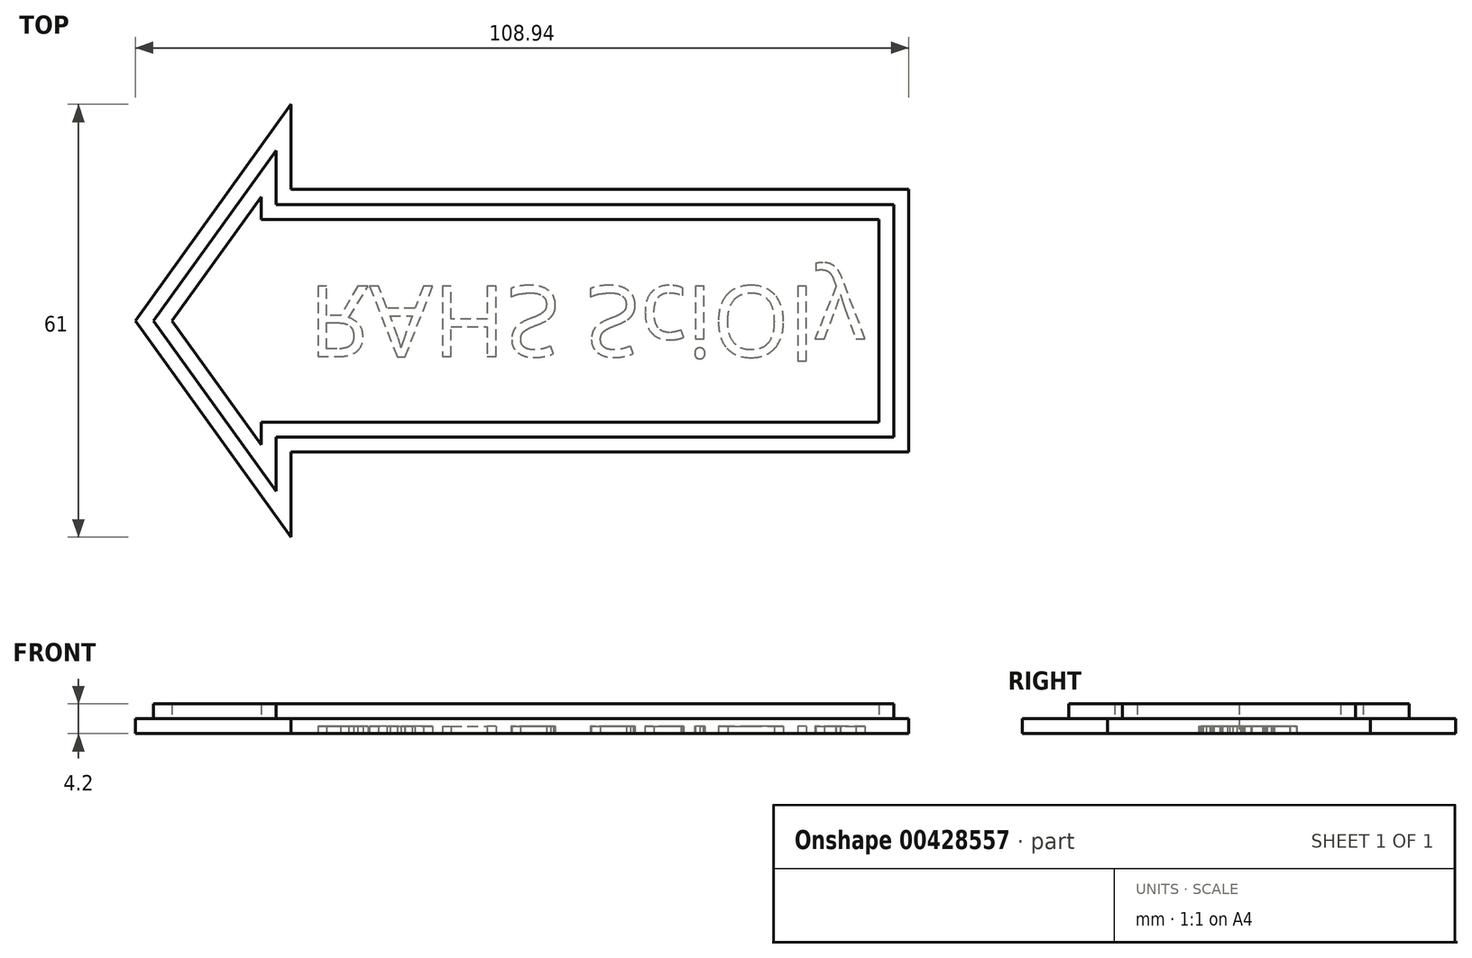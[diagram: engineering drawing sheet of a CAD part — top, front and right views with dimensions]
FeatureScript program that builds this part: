
annotation { "Feature Type Name" : "Feature", "Feature Type Description" : "" }
export const myFeature = defineFeature(function(context is Context, id is Id, definition is map)
    precondition{}
    {
        {
            var Q0;
            Q0=qCreatedBy(makeId("Top.planeOp"),FACE);
            var sketch = newSketch(context, id + "F0", { "sketchPlane" : qUnion([Q0])});
            skLineSegment(sketch, "E0.0", {"start": v(61.6, 18.5) * mm, "end": v(61.6, -18.5) * mm});
            skLineSegment(sketch, "E0.1", {"start": v(-25.4, 18.5) * mm, "end": v(61.6, 18.5) * mm});
            skLineSegment(sketch, "E0.3", {"start": v(-25.4, -18.5) * mm, "end": v(61.6, -18.5) * mm});
            skLineSegment(sketch, "E1", {"start": v(-25.4, 18.5) * mm, "end": v(-25.4, 30.5) * mm});
            skLineSegment(sketch, "E2", {"start": v(-25.4, 30.5) * mm, "end": v(-47.35, 0) * mm});
            skLineSegment(sketch, "E3", {"start": v(-47.35, 0) * mm, "end": v(-25.4, -30.5) * mm});
            skLineSegment(sketch, "E4", {"start": v(-25.4, -30.5) * mm, "end": v(-25.4, -18.5) * mm});
            skPoint(sketch, "E5", {"position": v(61.6, 0) * mm});
            skSolve(sketch);
        }
        {
            var Q0;
            Q0=makeQuery(id+"F0.imprint","IMPRINT",FACE,{"disambiguationData":[TD([[makeQuery(id+"F0.imprint","IMPRINT",EDGE,{"derivedFrom":sQuery(id+"F0.wireOp",EDGE,"E0.0")}),-1.0]])]});
            extrude(context, id + "F1", {"entities" : qUnion([Q0]), "depth" : 2.1 * mm});
        }
        {
            var Q0;
            Q0=makeQuery(id+"F1.opExtrude","CAP_FACE",FACE,{"disambiguationData":[OSD([sQuery(id+"F0.wireOp",EDGE,"E0.0"),sQuery(id+"F0.wireOp",EDGE,"E0.1"),sQuery(id+"F0.wireOp",EDGE,"E0.3"),sQuery(id+"F0.wireOp",EDGE,"E1"),sQuery(id+"F0.wireOp",EDGE,"E2"),sQuery(id+"F0.wireOp",EDGE,"E3"),sQuery(id+"F0.wireOp",EDGE,"E4")])],"isStart":false});
            var sketch = newSketch(context, id + "F2", { "sketchPlane" : qUnion([Q0])});
            skLineSegment(sketch, "E6.0", {"start": v(61.6, 18.5) * mm, "end": v(61.6, -18.5) * mm, "construction": true});
            skLineSegment(sketch, "E6.1", {"start": v(-25.4, 18.5) * mm, "end": v(61.6, 18.5) * mm, "construction": true});
            skLineSegment(sketch, "E6.3", {"start": v(-25.4, -18.5) * mm, "end": v(61.6, -18.5) * mm, "construction": true});
            skLineSegment(sketch, "E7", {"start": v(-25.4, 18.5) * mm, "end": v(-25.4, 30.5) * mm, "construction": true});
            skLineSegment(sketch, "E8", {"start": v(-25.4, 30.5) * mm, "end": v(-47.35, 0) * mm, "construction": true});
            skLineSegment(sketch, "E9", {"start": v(-47.35, 0) * mm, "end": v(-25.4, -30.5) * mm, "construction": true});
            skLineSegment(sketch, "E10", {"start": v(-25.4, -30.5) * mm, "end": v(-25.4, -18.5) * mm, "construction": true});
            skPoint(sketch, "E11", {"position": v(61.6, 0) * mm});
            skLineSegment(sketch, "E12.0", {"start": v(-27.5, 16.4) * mm, "end": v(-27.5, 23.99) * mm});
            skLineSegment(sketch, "E12.1", {"start": v(-27.5, 16.4) * mm, "end": v(59.5, 16.4) * mm});
            skLineSegment(sketch, "E12.2", {"start": v(-44.77, 0) * mm, "end": v(-27.5, -23.99) * mm});
            skLineSegment(sketch, "E12.3", {"start": v(-27.5, -23.99) * mm, "end": v(-27.5, -16.4) * mm});
            skLineSegment(sketch, "E12.4", {"start": v(-27.5, -16.4) * mm, "end": v(59.5, -16.4) * mm});
            skLineSegment(sketch, "E12.5", {"start": v(-27.5, 23.99) * mm, "end": v(-44.77, 0) * mm});
            skLineSegment(sketch, "E12.6", {"start": v(59.5, 16.4) * mm, "end": v(59.5, -16.4) * mm});
            skLineSegment(sketch, "E13.0", {"start": v(-29.6, 14.3) * mm, "end": v(-29.6, 17.47) * mm});
            skLineSegment(sketch, "E13.1", {"start": v(-29.6, 14.3) * mm, "end": v(57.4, 14.3) * mm});
            skLineSegment(sketch, "E13.2", {"start": v(-42.18, 0) * mm, "end": v(-29.6, -17.47) * mm});
            skLineSegment(sketch, "E13.3", {"start": v(-29.6, -17.47) * mm, "end": v(-29.6, -14.3) * mm});
            skLineSegment(sketch, "E13.4", {"start": v(-29.6, -14.3) * mm, "end": v(57.4, -14.3) * mm});
            skLineSegment(sketch, "E13.5", {"start": v(-29.6, 17.47) * mm, "end": v(-42.18, 0) * mm});
            skLineSegment(sketch, "E13.6", {"start": v(57.4, 14.3) * mm, "end": v(57.4, -14.3) * mm});
            skLineSegment(sketch, "E14", {"start": v(59.5, 0) * mm, "end": v(-15, 0) * mm, "construction": true});
            skPoint(sketch, "E14.endSnap0", {"position": v(59.5, 0) * mm});
            skSolve(sketch);
        }
        {
            var Q0;
            Q0=makeQuery(id+"F2.imprint","IMPRINT",FACE,{"disambiguationData":[TD([[makeQuery(id+"F2.imprint","IMPRINT",EDGE,{"derivedFrom":sQuery(id+"F2.wireOp",EDGE,"E12.0")}),1.0]])]});
            extrude(context, id + "F3", {"entities" : qUnion([Q0]), "operationType" : NewBodyOperationType.ADD, "depth" : 2.1 * mm});
        }
        {
            var Q0;
            Q0=makeQuery(id+"F1.opExtrude","CAP_FACE",FACE,{"disambiguationData":[OSD([sQuery(id+"F0.wireOp",EDGE,"E0.0"),sQuery(id+"F0.wireOp",EDGE,"E0.1"),sQuery(id+"F0.wireOp",EDGE,"E0.3"),sQuery(id+"F0.wireOp",EDGE,"E1"),sQuery(id+"F0.wireOp",EDGE,"E2"),sQuery(id+"F0.wireOp",EDGE,"E3"),sQuery(id+"F0.wireOp",EDGE,"E4")])],"isStart":true});
            var sketch = newSketch(context, id + "F4", { "sketchPlane" : qUnion([Q0])});
            skText(sketch, "E15", { "text": "RAHS SciOly", "fontName": "NotoSans-Regular.ttf"});
            const initialGuessF4  = {"E15": [-0.02298, -0.00487, 1, 0, 0.01]};
            skSetInitialGuess(sketch, initialGuessF4);
            skSolve(sketch);
        }
        {
            var Q0;
            Q0 = qSketchRegion(id + "F4", true);
            extrude(context, id + "F5", {"entities" : qUnion([Q0]), "operationType" : NewBodyOperationType.REMOVE, "oppositeDirection" : true, "depth" : 1.02 * mm, "offsetDistance" : 25 * mm});
        }
    });
